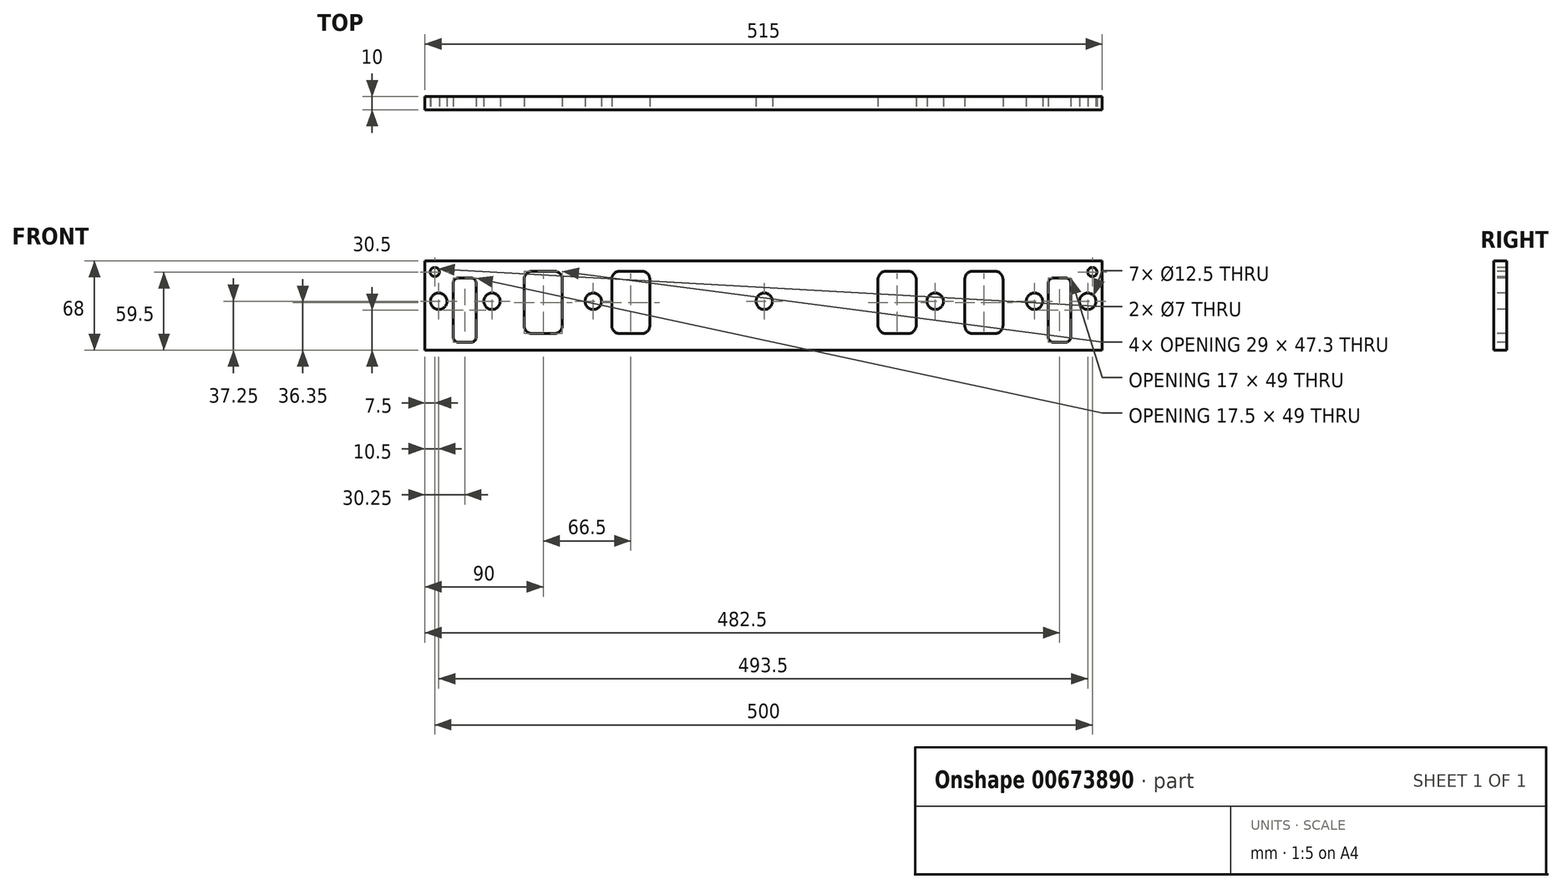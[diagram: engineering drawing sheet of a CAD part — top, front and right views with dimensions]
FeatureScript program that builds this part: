
annotation { "Feature Type Name" : "Feature", "Feature Type Description" : "" }
export const myFeature = defineFeature(function(context is Context, id is Id, definition is map)
    precondition{}
    {
        {
            var Q0;
            Q0=qCreatedBy(makeId("Front.planeOp"),FACE);
            var sketch = newSketch(context, id + "F0", { "sketchPlane" : qUnion([Q0])});
            skLineSegment(sketch, "E0.bottom", {"start": v(0, 0) * mm, "end": v(515, 0) * mm});
            skLineSegment(sketch, "E0.top", {"start": v(0, -68) * mm, "end": v(515, -68) * mm});
            skLineSegment(sketch, "E0.left", {"start": v(0, 0) * mm, "end": v(0, -68) * mm});
            skLineSegment(sketch, "E0.right", {"start": v(515, 0) * mm, "end": v(515, -68) * mm});
            skSolve(sketch);
        }
        {
            var Q0;
            Q0=makeQuery(id+"F0.imprint","IMPRINT",FACE,{"disambiguationData":[TD([[makeQuery(id+"F0.imprint","IMPRINT",EDGE,{"derivedFrom":sQuery(id+"F0.wireOp",EDGE,"E0.bottom")}),-1.0]])]});
            extrude(context, id + "F1", {"entities" : qUnion([Q0]), "depth" : 10 * mm, "offsetDistance" : 25 * mm});
        }
        {
            var Q0;
            Q0=makeQuery(id+"F1.opExtrude","CAP_FACE",FACE,{"disambiguationData":[OSD([sQuery(id+"F0.wireOp",EDGE,"E0.bottom"),sQuery(id+"F0.wireOp",EDGE,"E0.top"),sQuery(id+"F0.wireOp",EDGE,"E0.left"),sQuery(id+"F0.wireOp",EDGE,"E0.right")])],"isStart":false});
            var sketch = newSketch(context, id + "F2", { "sketchPlane" : qUnion([Q0])});
            skCircle(sketch, "E1", {"center": v(7.5, -8.5) * mm, "radius": 3.5 * mm});
            skCircle(sketch, "E2", {"center": v(507.5, -8.5) * mm, "radius": 3.5 * mm});
            skCircle(sketch, "E3", {"center": v(10.5, -30.75) * mm, "radius": 6.25 * mm});
            skCircle(sketch, "E4", {"center": v(51, -30.75) * mm, "radius": 6.25 * mm});
            skCircle(sketch, "E5", {"center": v(128, -30.75) * mm, "radius": 6.25 * mm});
            skCircle(sketch, "E6", {"center": v(258, -30.75) * mm, "radius": 6.25 * mm});
            skCircle(sketch, "E7", {"center": v(388, -30.75) * mm, "radius": 6.25 * mm});
            skCircle(sketch, "E8", {"center": v(463.5, -30.75) * mm, "radius": 6.25 * mm});
            skCircle(sketch, "E9", {"center": v(504, -30.75) * mm, "radius": 6.25 * mm});
            skSolve(sketch);
        }
        {
            var Q0;
            Q0 = qSketchRegion(id + "F2", true);
            extrude(context, id + "F3", {"entities" : qUnion([Q0]), "operationType" : NewBodyOperationType.REMOVE, "endBound" : BoundingType.THROUGH_ALL, "oppositeDirection" : true, "depth" : 25 * mm, "offsetDistance" : 25 * mm});
        }
        {
            var Q0;
            Q0=makeQuery(id+"F1.opExtrude","CAP_FACE",FACE,{"disambiguationData":[OSD([sQuery(id+"F0.wireOp",EDGE,"E0.bottom"),sQuery(id+"F0.wireOp",EDGE,"E0.top"),sQuery(id+"F0.wireOp",EDGE,"E0.left"),sQuery(id+"F0.wireOp",EDGE,"E0.right")])],"isStart":false});
            var sketch = newSketch(context, id + "F4", { "sketchPlane" : qUnion([Q0])});
            skLineSegment(sketch, "E10.bottom", {"start": v(21.5, -13) * mm, "end": v(39, -13) * mm});
            skLineSegment(sketch, "E10.top", {"start": v(21.5, -62) * mm, "end": v(39, -62) * mm});
            skLineSegment(sketch, "E10.left", {"start": v(21.5, -13) * mm, "end": v(21.5, -62) * mm});
            skLineSegment(sketch, "E10.right", {"start": v(39, -13) * mm, "end": v(39, -62) * mm});
            skLineSegment(sketch, "E11.bottom", {"start": v(75.5, -8) * mm, "end": v(104.5, -8) * mm});
            skLineSegment(sketch, "E11.top", {"start": v(75.5, -55.3) * mm, "end": v(104.5, -55.3) * mm});
            skLineSegment(sketch, "E11.left", {"start": v(75.5, -8) * mm, "end": v(75.5, -55.3) * mm});
            skLineSegment(sketch, "E11.right", {"start": v(104.5, -8) * mm, "end": v(104.5, -55.3) * mm});
            skLineSegment(sketch, "E12.bottom", {"start": v(142, -8) * mm, "end": v(171, -8) * mm});
            skLineSegment(sketch, "E12.top", {"start": v(142, -55.3) * mm, "end": v(171, -55.3) * mm});
            skLineSegment(sketch, "E12.left", {"start": v(142, -8) * mm, "end": v(142, -55.3) * mm});
            skLineSegment(sketch, "E12.right", {"start": v(171, -8) * mm, "end": v(171, -55.3) * mm});
            skLineSegment(sketch, "E13.bottom", {"start": v(344.5, -8) * mm, "end": v(373.5, -8) * mm});
            skLineSegment(sketch, "E13.top", {"start": v(344.5, -55.3) * mm, "end": v(373.5, -55.3) * mm});
            skLineSegment(sketch, "E13.left", {"start": v(344.5, -8) * mm, "end": v(344.5, -55.3) * mm});
            skLineSegment(sketch, "E13.right", {"start": v(373.5, -8) * mm, "end": v(373.5, -55.3) * mm});
            skLineSegment(sketch, "E14.bottom", {"start": v(410.5, -8) * mm, "end": v(439.5, -8) * mm});
            skLineSegment(sketch, "E14.top", {"start": v(410.5, -55.3) * mm, "end": v(439.5, -55.3) * mm});
            skLineSegment(sketch, "E14.left", {"start": v(410.5, -8) * mm, "end": v(410.5, -55.3) * mm});
            skLineSegment(sketch, "E14.right", {"start": v(439.5, -8) * mm, "end": v(439.5, -55.3) * mm});
            skLineSegment(sketch, "E15.bottom", {"start": v(474, -13) * mm, "end": v(491, -13) * mm});
            skLineSegment(sketch, "E15.top", {"start": v(474, -62) * mm, "end": v(491, -62) * mm});
            skLineSegment(sketch, "E15.left", {"start": v(474, -13) * mm, "end": v(474, -62) * mm});
            skLineSegment(sketch, "E15.right", {"start": v(491, -13) * mm, "end": v(491, -62) * mm});
            skSolve(sketch);
        }
        {
            var Q0;
            Q0=makeQuery(id+"F4.imprint","IMPRINT",FACE,{"disambiguationData":[TD([[makeQuery(id+"F4.imprint","IMPRINT",EDGE,{"derivedFrom":sQuery(id+"F4.wireOp",EDGE,"E10.bottom")}),-1.0]])]});
            var Q1;
            Q1=makeQuery(id+"F4.imprint","IMPRINT",FACE,{"disambiguationData":[TD([[makeQuery(id+"F4.imprint","IMPRINT",EDGE,{"derivedFrom":sQuery(id+"F4.wireOp",EDGE,"E15.bottom")}),-1.0]])]});
            extrude(context, id + "F5", {"entities" : qUnion([Q0, Q1]), "operationType" : NewBodyOperationType.REMOVE, "endBound" : BoundingType.THROUGH_ALL, "oppositeDirection" : true, "depth" : 25 * mm, "offsetDistance" : 25 * mm});
        }
        {
            var Q0;
            Q0=makeQuery(id+"F4.imprint","IMPRINT",FACE,{"disambiguationData":[TD([[makeQuery(id+"F4.imprint","IMPRINT",EDGE,{"derivedFrom":sQuery(id+"F4.wireOp",EDGE,"E11.bottom")}),-1.0]])]});
            var Q1;
            Q1=makeQuery(id+"F4.imprint","IMPRINT",FACE,{"disambiguationData":[TD([[makeQuery(id+"F4.imprint","IMPRINT",EDGE,{"derivedFrom":sQuery(id+"F4.wireOp",EDGE,"E12.bottom")}),-1.0]])]});
            var Q2;
            Q2=makeQuery(id+"F4.imprint","IMPRINT",FACE,{"disambiguationData":[TD([[makeQuery(id+"F4.imprint","IMPRINT",EDGE,{"derivedFrom":sQuery(id+"F4.wireOp",EDGE,"E13.bottom")}),-1.0]])]});
            var Q3;
            Q3=makeQuery(id+"F4.imprint","IMPRINT",FACE,{"disambiguationData":[TD([[makeQuery(id+"F4.imprint","IMPRINT",EDGE,{"derivedFrom":sQuery(id+"F4.wireOp",EDGE,"E14.bottom")}),-1.0]])]});
            extrude(context, id + "F6", {"entities" : qUnion([Q0, Q1, Q2, Q3]), "operationType" : NewBodyOperationType.REMOVE, "endBound" : BoundingType.THROUGH_ALL, "oppositeDirection" : true, "depth" : 25 * mm, "offsetDistance" : 25 * mm});
        }
        {
            var Q0;
            Q0=makeQuery(id+"F5.boolean.opBoolean","COPY",EDGE,{"derivedFrom":makeQuery(id+"F5.opExtrude","SWEPT_EDGE",EDGE,{"disambiguationData":[OSD([sQuery(id+"F4.wireOp",EDGE,"E10.bottom"),sQuery(id+"F4.wireOp",EDGE,"E10.left")])]})});
            var Q1;
            Q1=makeQuery(id+"F5.boolean.opBoolean","COPY",EDGE,{"derivedFrom":makeQuery(id+"F5.opExtrude","SWEPT_EDGE",EDGE,{"disambiguationData":[OSD([sQuery(id+"F4.wireOp",EDGE,"E10.top"),sQuery(id+"F4.wireOp",EDGE,"E10.left")])]})});
            var Q2;
            Q2=makeQuery(id+"F5.boolean.opBoolean","COPY",EDGE,{"derivedFrom":makeQuery(id+"F5.opExtrude","SWEPT_EDGE",EDGE,{"disambiguationData":[OSD([sQuery(id+"F4.wireOp",EDGE,"E10.top"),sQuery(id+"F4.wireOp",EDGE,"E10.right")])]})});
            var Q3;
            Q3=makeQuery(id+"F5.boolean.opBoolean","COPY",EDGE,{"derivedFrom":makeQuery(id+"F5.opExtrude","SWEPT_EDGE",EDGE,{"disambiguationData":[OSD([sQuery(id+"F4.wireOp",EDGE,"E10.bottom"),sQuery(id+"F4.wireOp",EDGE,"E10.right")])]})});
            var Q4;
            Q4=makeQuery(id+"F5.boolean.opBoolean","COPY",EDGE,{"derivedFrom":makeQuery(id+"F5.opExtrude","SWEPT_EDGE",EDGE,{"disambiguationData":[OSD([sQuery(id+"F4.wireOp",EDGE,"E15.bottom"),sQuery(id+"F4.wireOp",EDGE,"E15.right")])]})});
            var Q5;
            Q5=makeQuery(id+"F5.boolean.opBoolean","COPY",EDGE,{"derivedFrom":makeQuery(id+"F5.opExtrude","SWEPT_EDGE",EDGE,{"disambiguationData":[OSD([sQuery(id+"F4.wireOp",EDGE,"E15.bottom"),sQuery(id+"F4.wireOp",EDGE,"E15.left")])]})});
            var Q6;
            Q6=makeQuery(id+"F5.boolean.opBoolean","COPY",EDGE,{"derivedFrom":makeQuery(id+"F5.opExtrude","SWEPT_EDGE",EDGE,{"disambiguationData":[OSD([sQuery(id+"F4.wireOp",EDGE,"E15.top"),sQuery(id+"F4.wireOp",EDGE,"E15.left")])]})});
            var Q7;
            Q7=makeQuery(id+"F5.boolean.opBoolean","COPY",EDGE,{"derivedFrom":makeQuery(id+"F5.opExtrude","SWEPT_EDGE",EDGE,{"disambiguationData":[OSD([sQuery(id+"F4.wireOp",EDGE,"E15.top"),sQuery(id+"F4.wireOp",EDGE,"E15.right")])]})});
            fillet(context, id + "F7", {"entities" : qUnion([Q0, Q1, Q2, Q3, Q4, Q5, Q6, Q7]), "radius" : 4 * mm, "tangentPropagation" : true, "allowEdgeOverflow" : false});
        }
        {
            var Q0;
            Q0=makeQuery(id+"F6.boolean.opBoolean","COPY",EDGE,{"derivedFrom":makeQuery(id+"F6.opExtrude","SWEPT_EDGE",EDGE,{"disambiguationData":[OSD([sQuery(id+"F4.wireOp",EDGE,"E14.bottom"),sQuery(id+"F4.wireOp",EDGE,"E14.left")])]})});
            var Q1;
            Q1=makeQuery(id+"F6.boolean.opBoolean","COPY",EDGE,{"derivedFrom":makeQuery(id+"F6.opExtrude","SWEPT_EDGE",EDGE,{"disambiguationData":[OSD([sQuery(id+"F4.wireOp",EDGE,"E14.bottom"),sQuery(id+"F4.wireOp",EDGE,"E14.right")])]})});
            var Q2;
            Q2=makeQuery(id+"F6.boolean.opBoolean","COPY",EDGE,{"derivedFrom":makeQuery(id+"F6.opExtrude","SWEPT_EDGE",EDGE,{"disambiguationData":[OSD([sQuery(id+"F4.wireOp",EDGE,"E11.bottom"),sQuery(id+"F4.wireOp",EDGE,"E11.left")])]})});
            var Q3;
            Q3=makeQuery(id+"F6.boolean.opBoolean","COPY",EDGE,{"derivedFrom":makeQuery(id+"F6.opExtrude","SWEPT_EDGE",EDGE,{"disambiguationData":[OSD([sQuery(id+"F4.wireOp",EDGE,"E11.bottom"),sQuery(id+"F4.wireOp",EDGE,"E11.right")])]})});
            var Q4;
            Q4=makeQuery(id+"F6.boolean.opBoolean","COPY",EDGE,{"derivedFrom":makeQuery(id+"F6.opExtrude","SWEPT_EDGE",EDGE,{"disambiguationData":[OSD([sQuery(id+"F4.wireOp",EDGE,"E12.bottom"),sQuery(id+"F4.wireOp",EDGE,"E12.right")])]})});
            var Q5;
            Q5=makeQuery(id+"F6.boolean.opBoolean","COPY",EDGE,{"derivedFrom":makeQuery(id+"F6.opExtrude","SWEPT_EDGE",EDGE,{"disambiguationData":[OSD([sQuery(id+"F4.wireOp",EDGE,"E11.top"),sQuery(id+"F4.wireOp",EDGE,"E11.left")])]})});
            var Q6;
            Q6=makeQuery(id+"F6.boolean.opBoolean","COPY",EDGE,{"derivedFrom":makeQuery(id+"F6.opExtrude","SWEPT_EDGE",EDGE,{"disambiguationData":[OSD([sQuery(id+"F4.wireOp",EDGE,"E12.top"),sQuery(id+"F4.wireOp",EDGE,"E12.left")])]})});
            var Q7;
            Q7=makeQuery(id+"F6.boolean.opBoolean","COPY",EDGE,{"derivedFrom":makeQuery(id+"F6.opExtrude","SWEPT_EDGE",EDGE,{"disambiguationData":[OSD([sQuery(id+"F4.wireOp",EDGE,"E12.bottom"),sQuery(id+"F4.wireOp",EDGE,"E12.left")])]})});
            var Q8;
            Q8=makeQuery(id+"F6.boolean.opBoolean","COPY",EDGE,{"derivedFrom":makeQuery(id+"F6.opExtrude","SWEPT_EDGE",EDGE,{"disambiguationData":[OSD([sQuery(id+"F4.wireOp",EDGE,"E12.top"),sQuery(id+"F4.wireOp",EDGE,"E12.right")])]})});
            var Q9;
            Q9=makeQuery(id+"F6.boolean.opBoolean","COPY",EDGE,{"derivedFrom":makeQuery(id+"F6.opExtrude","SWEPT_EDGE",EDGE,{"disambiguationData":[OSD([sQuery(id+"F4.wireOp",EDGE,"E11.top"),sQuery(id+"F4.wireOp",EDGE,"E11.right")])]})});
            var Q10;
            Q10=makeQuery(id+"F6.boolean.opBoolean","COPY",EDGE,{"derivedFrom":makeQuery(id+"F6.opExtrude","SWEPT_EDGE",EDGE,{"disambiguationData":[OSD([sQuery(id+"F4.wireOp",EDGE,"E14.top"),sQuery(id+"F4.wireOp",EDGE,"E14.right")])]})});
            var Q11;
            Q11=makeQuery(id+"F6.boolean.opBoolean","COPY",EDGE,{"derivedFrom":makeQuery(id+"F6.opExtrude","SWEPT_EDGE",EDGE,{"disambiguationData":[OSD([sQuery(id+"F4.wireOp",EDGE,"E13.top"),sQuery(id+"F4.wireOp",EDGE,"E13.right")])]})});
            var Q12;
            Q12=makeQuery(id+"F6.boolean.opBoolean","COPY",EDGE,{"derivedFrom":makeQuery(id+"F6.opExtrude","SWEPT_EDGE",EDGE,{"disambiguationData":[OSD([sQuery(id+"F4.wireOp",EDGE,"E14.top"),sQuery(id+"F4.wireOp",EDGE,"E14.left")])]})});
            var Q13;
            Q13=makeQuery(id+"F6.boolean.opBoolean","COPY",EDGE,{"derivedFrom":makeQuery(id+"F6.opExtrude","SWEPT_EDGE",EDGE,{"disambiguationData":[OSD([sQuery(id+"F4.wireOp",EDGE,"E13.top"),sQuery(id+"F4.wireOp",EDGE,"E13.left")])]})});
            var Q14;
            Q14=makeQuery(id+"F6.boolean.opBoolean","COPY",EDGE,{"derivedFrom":makeQuery(id+"F6.opExtrude","SWEPT_EDGE",EDGE,{"disambiguationData":[OSD([sQuery(id+"F4.wireOp",EDGE,"E13.bottom"),sQuery(id+"F4.wireOp",EDGE,"E13.right")])]})});
            var Q15;
            Q15=makeQuery(id+"F6.boolean.opBoolean","COPY",EDGE,{"derivedFrom":makeQuery(id+"F6.opExtrude","SWEPT_EDGE",EDGE,{"disambiguationData":[OSD([sQuery(id+"F4.wireOp",EDGE,"E13.bottom"),sQuery(id+"F4.wireOp",EDGE,"E13.left")])]})});
            fillet(context, id + "F8", {"entities" : qUnion([Q0, Q1, Q2, Q3, Q4, Q5, Q6, Q7, Q8, Q9, Q10, Q11, Q12, Q13, Q14, Q15]), "radius" : 6 * mm, "tangentPropagation" : true, "allowEdgeOverflow" : false});
        }
    });
